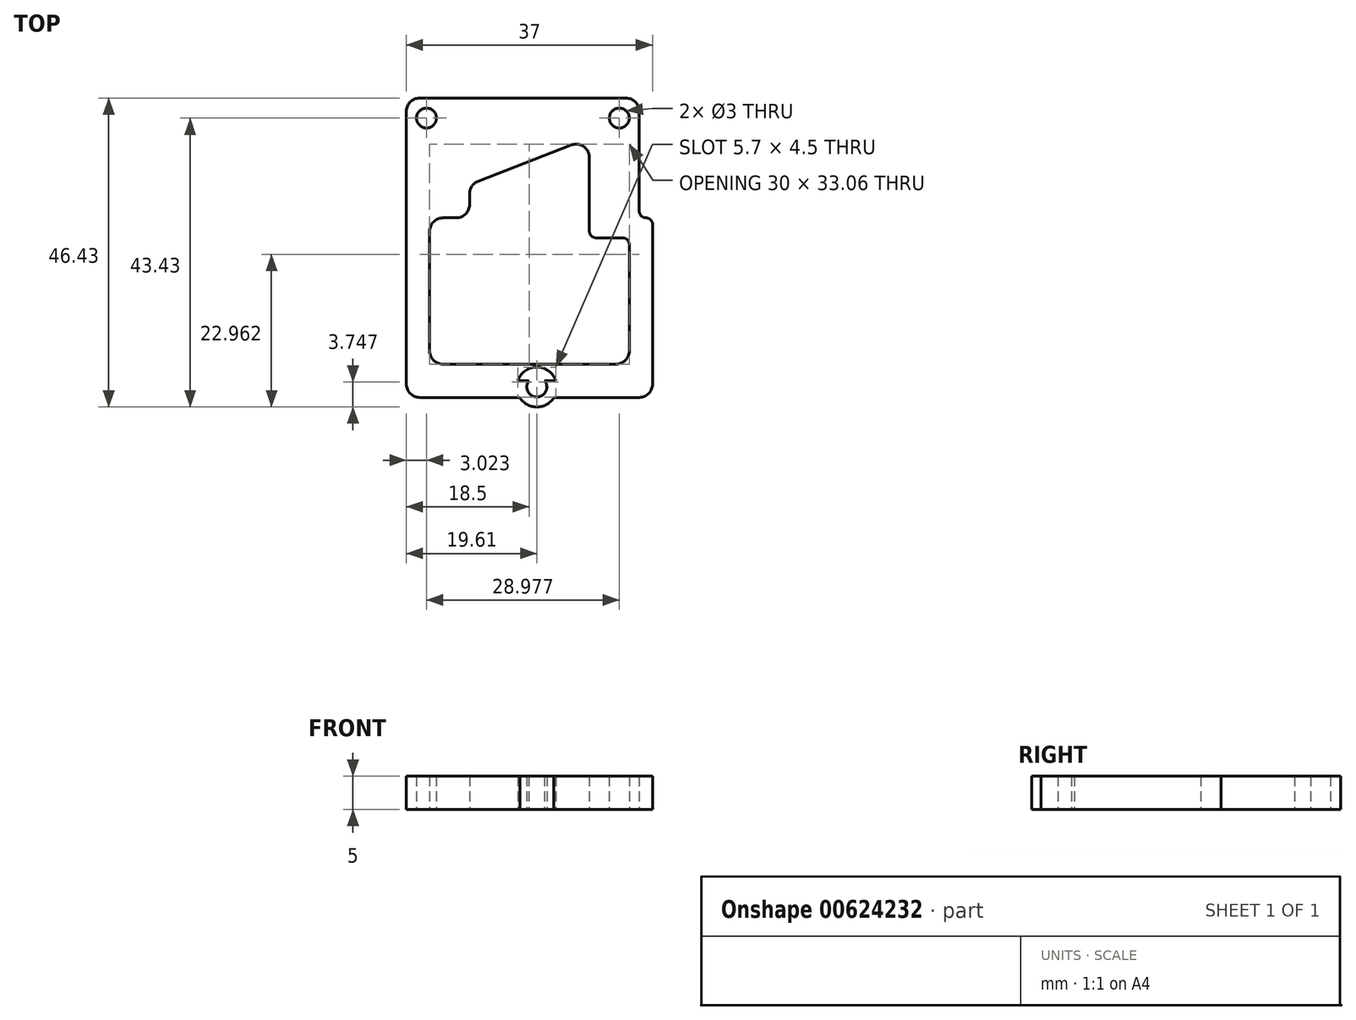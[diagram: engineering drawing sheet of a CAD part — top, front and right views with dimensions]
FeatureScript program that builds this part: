
annotation { "Feature Type Name" : "Feature", "Feature Type Description" : "" }
export const myFeature = defineFeature(function(context is Context, id is Id, definition is map)
    precondition{}
    {
        {
            var Q0;
            Q0=qCreatedBy(makeId("Top.planeOp"),FACE);
            var sketch = newSketch(context, id + "F0", { "sketchPlane" : qUnion([Q0])});
            skLineSegment(sketch, "E0.bottom", {"start": v(14.5, 22.5) * mm, "end": v(-16.5, 22.5) * mm});
            skLineSegment(sketch, "E0.top", {"start": v(16.5, -22.5) * mm, "end": v(-16.5, -22.5) * mm});
            skLineSegment(sketch, "E0.left", {"start": v(18.5, 3.5) * mm, "end": v(18.5, -20.5) * mm});
            skLineSegment(sketch, "E0.right", {"start": v(-18.5, 20.5) * mm, "end": v(-18.5, -20.5) * mm});
            skPoint(sketch, "E0.middle", {"position": v(0, 0) * mm});
            skLineSegment(sketch, "E1", {"start": v(-15, 2.5) * mm, "end": v(-15, -15.5) * mm});
            skLineSegment(sketch, "E2", {"start": v(-13, -17.5) * mm, "end": v(13, -17.5) * mm});
            skLineSegment(sketch, "E3", {"start": v(15, -15.5) * mm, "end": v(15, 0.5) * mm});
            skLineSegment(sketch, "E4", {"start": v(-13, 4.5) * mm, "end": v(-11, 4.5) * mm});
            skLineSegment(sketch, "E5", {"start": v(-9, 6.5) * mm, "end": v(-9, 8.13) * mm});
            skLineSegment(sketch, "E6", {"start": v(-7.72, 10) * mm, "end": v(6.28, 15.44) * mm});
            skLineSegment(sketch, "E7", {"start": v(9, 13.58) * mm, "end": v(9, 2.5) * mm});
            skLineSegment(sketch, "E8", {"start": v(10, 1.5) * mm, "end": v(14, 1.5) * mm});
            skLineSegment(sketch, "E9", {"start": v(16.5, 20.5) * mm, "end": v(16.5, 5.5) * mm});
            skLineSegment(sketch, "E10", {"start": v(17.5, 4.5) * mm, "end": v(17.5, 4.5) * mm});
            skPoint(sketch, "E11.visualSharp", {"position": v(9, 16.5) * mm});
            skArc(sketch, "E11.filletArc", {"start": v(9, 13.58) * mm, "mid": v(8.13, 15.23) * mm, "end": v(6.28, 15.44) * mm});
            skPoint(sketch, "E12.visualSharp", {"position": v(-15, 4.5) * mm});
            skArc(sketch, "E12.filletArc", {"start": v(-13, 4.5) * mm, "mid": v(-14.41, 3.91) * mm, "end": v(-15, 2.5) * mm});
            skPoint(sketch, "E13.visualSharp", {"position": v(-15, -17.5) * mm});
            skArc(sketch, "E13.filletArc", {"start": v(-15, -15.5) * mm, "mid": v(-14.41, -16.91) * mm, "end": v(-13, -17.5) * mm});
            skPoint(sketch, "E14.visualSharp", {"position": v(15, -17.5) * mm});
            skArc(sketch, "E14.filletArc", {"start": v(13, -17.5) * mm, "mid": v(14.41, -16.91) * mm, "end": v(15, -15.5) * mm});
            skPoint(sketch, "E15.visualSharp", {"position": v(-9, 4.5) * mm});
            skArc(sketch, "E15.filletArc", {"start": v(-11, 4.5) * mm, "mid": v(-9.59, 5.09) * mm, "end": v(-9, 6.5) * mm});
            skPoint(sketch, "E16.visualSharp", {"position": v(-9, 9.5) * mm});
            skArc(sketch, "E16.filletArc", {"start": v(-7.72, 10) * mm, "mid": v(-8.65, 9.26) * mm, "end": v(-9, 8.13) * mm});
            skPoint(sketch, "E17.visualSharp", {"position": v(-18.5, -22.5) * mm});
            skArc(sketch, "E17.filletArc", {"start": v(-18.5, -20.5) * mm, "mid": v(-17.91, -21.91) * mm, "end": v(-16.5, -22.5) * mm});
            skPoint(sketch, "E18.visualSharp", {"position": v(18.5, -22.5) * mm});
            skArc(sketch, "E18.filletArc", {"start": v(16.5, -22.5) * mm, "mid": v(17.91, -21.91) * mm, "end": v(18.5, -20.5) * mm});
            skPoint(sketch, "E19.visualSharp", {"position": v(18.5, 22.5) * mm});
            skPoint(sketch, "E20.visualSharp", {"position": v(-18.5, 22.5) * mm});
            skArc(sketch, "E20.filletArc", {"start": v(-16.5, 22.5) * mm, "mid": v(-17.91, 21.91) * mm, "end": v(-18.5, 20.5) * mm});
            skPoint(sketch, "E21.visualSharp", {"position": v(16.5, 22.5) * mm});
            skArc(sketch, "E21.filletArc", {"start": v(16.5, 20.5) * mm, "mid": v(15.91, 21.91) * mm, "end": v(14.5, 22.5) * mm});
            skPoint(sketch, "E22.visualSharp", {"position": v(18.5, 4.5) * mm});
            skArc(sketch, "E22.filletArc", {"start": v(18.5, 3.5) * mm, "mid": v(18.2, 4.2) * mm, "end": v(17.5, 4.5) * mm});
            skPoint(sketch, "E23.visualSharp", {"position": v(16.5, 4.5) * mm});
            skArc(sketch, "E23.filletArc", {"start": v(16.5, 5.5) * mm, "mid": v(16.8, 4.8) * mm, "end": v(17.5, 4.5) * mm});
            skPoint(sketch, "E24.visualSharp", {"position": v(9, 1.5) * mm});
            skArc(sketch, "E24.filletArc", {"start": v(9, 2.5) * mm, "mid": v(9.3, 1.8) * mm, "end": v(10, 1.5) * mm});
            skPoint(sketch, "E25.visualSharp", {"position": v(15, 1.5) * mm});
            skArc(sketch, "E25.filletArc", {"start": v(15, 0.5) * mm, "mid": v(14.7, 1.2) * mm, "end": v(14, 1.5) * mm});
            skLineSegment(sketch, "E26", {"start": v(-14, -20) * mm, "end": v(14, -20) * mm});
            skLineSegment(sketch, "E27", {"start": v(-15, -15.5) * mm, "end": v(-15, -19) * mm});
            skLineSegment(sketch, "E28", {"start": v(15, -15.5) * mm, "end": v(15, -19) * mm});
            skPoint(sketch, "E29.orphan", {"position": v(15.54, -20) * mm});
            skPoint(sketch, "E30.visualSharp", {"position": v(15, -20) * mm});
            skArc(sketch, "E30.filletArc", {"start": v(14, -20) * mm, "mid": v(14.7, -19.7) * mm, "end": v(15, -19) * mm});
            skPoint(sketch, "E31.visualSharp", {"position": v(-15, -20) * mm});
            skArc(sketch, "E31.filletArc", {"start": v(-15, -19) * mm, "mid": v(-14.7, -19.7) * mm, "end": v(-14, -20) * mm});
            skLineSegment(sketch, "E32", {"start": v(1.1, -17.5) * mm, "end": v(1.1, -22.5) * mm, "construction": true});
            skCircle(sketch, "E33", {"center": v(1.1, -20.93) * mm, "radius": 3 * mm});
            skCircle(sketch, "E34", {"center": v(1.1, -20.93) * mm, "radius": 1.5 * mm});
            skLineSegment(sketch, "E35", {"start": v(-16.5, 19.5) * mm, "end": v(15.55, 19.5) * mm, "construction": true});
            skCircle(sketch, "E36", {"center": v(13.5, 19.5) * mm, "radius": 3 * mm});
            skCircle(sketch, "E37", {"center": v(13.5, 19.5) * mm, "radius": 1.5 * mm});
            skCircle(sketch, "E38", {"center": v(-15.48, 19.5) * mm, "radius": 3 * mm});
            skCircle(sketch, "E39", {"center": v(-15.48, 19.5) * mm, "radius": 1.5 * mm});
            skLineSegment(sketch, "E40", {"start": v(-18.5, -15.5) * mm, "end": v(-15, -15.5) * mm});
            skLineSegment(sketch, "E41", {"start": v(-18.5, 7.5) * mm, "end": v(-11.5, 7.5) * mm});
            skLineSegment(sketch, "E42", {"start": v(-11.5, 7.5) * mm, "end": v(-11.5, 22.5) * mm});
            skLineSegment(sketch, "E43", {"start": v(6.5, 15.53) * mm, "end": v(6.5, 22.5) * mm});
            skLineSegment(sketch, "E44", {"start": v(-6.75, 10.38) * mm, "end": v(-11.5, 8.53) * mm});
            skSolve(sketch);
        }
        {
            var Q0;
            Q0=makeQuery(id+"F0.imprint","IMPRINT",FACE,{"disambiguationData":[TD([[makeQuery(id+"F0.imprint","IMPRINT",EDGE,{"derivedFrom":sQuery(id+"F0.wireOp",EDGE,"E2")}),-1.0]])]});
            extrude(context, id + "F1", {"entities" : qUnion([Q0]), "depth" : 3 * mm, "offsetDistance" : 25 * mm});
        }
        {
            var Q0;
            Q0 = qSketchRegion(id + "F0", true);
            var Q1;
            {var subQ0=sQuery(id+"F0.wireOp",EDGE,"E33");var subQ1=sQuery(id+"F0.wireOp",EDGE,"E26");var subQ2=makeQuery(id+"F0.imprint","INTERSECT",VERTEX,{"disambiguationData":[OD(0.0)],"derivedFrom":[subQ1,subQ0]});Q1=makeQuery(id+"F0.imprint","IMPRINT",FACE,{"disambiguationData":[TD([[makeQuery(id+"F0.imprint","IMPRINT",EDGE,{"disambiguationData":[TD([[subQ2,-1.0]])],"derivedFrom":subQ1}),1.0]])]});}
            extrude(context, id + "F2", {"entities" : qUnion([Q0, Q1]), "operationType" : NewBodyOperationType.ADD, "depth" : 5 * mm, "offsetDistance" : 25 * mm});
        }
    });
